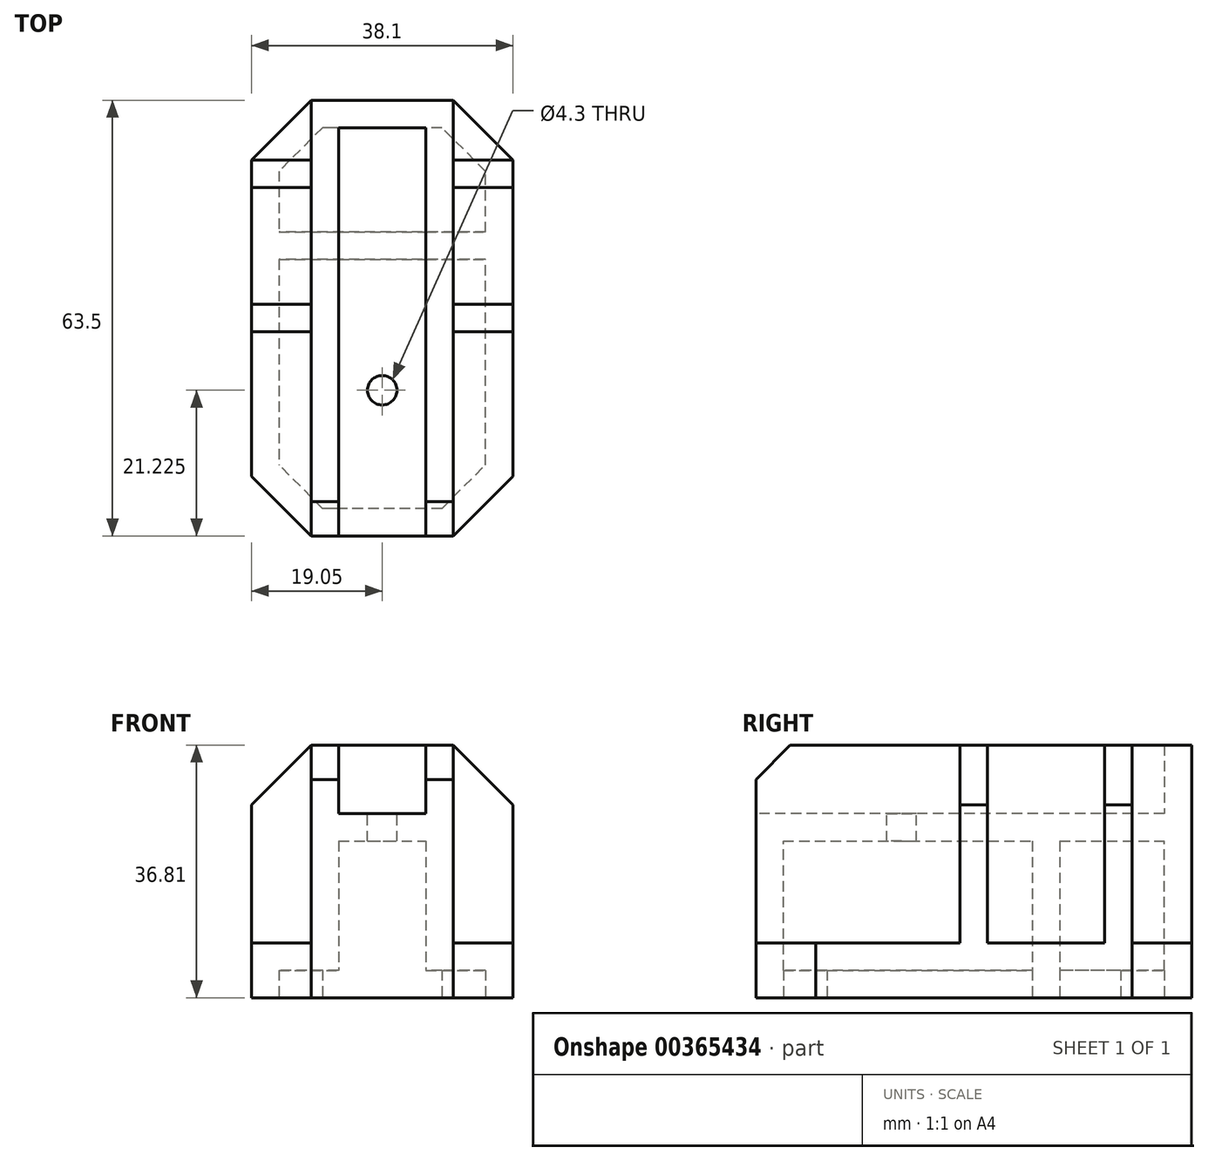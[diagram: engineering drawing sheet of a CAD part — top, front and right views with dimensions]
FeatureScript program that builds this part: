
annotation { "Feature Type Name" : "Feature", "Feature Type Description" : "" }
export const myFeature = defineFeature(function(context is Context, id is Id, definition is map)
    precondition{}
    {
        {
            var Q0;
            Q0=qCreatedBy(makeId("Front.planeOp"),FACE);
            var sketch = newSketch(context, id + "F0", { "sketchPlane" : qUnion([Q0])});
            skLineSegment(sketch, "E0.bottom", {"start": v(10.35, 0) * mm, "end": v(-10.35, 0) * mm});
            skLineSegment(sketch, "E0.top", {"start": v(10.35, 26.81) * mm, "end": v(-10.35, 26.81) * mm});
            skLineSegment(sketch, "E0.left", {"start": v(10.35, 0) * mm, "end": v(10.35, 26.81) * mm});
            skLineSegment(sketch, "E0.right", {"start": v(-10.35, 0) * mm, "end": v(-10.35, 26.81) * mm});
            skPoint(sketch, "E0.middle", {"position": v(0, 13.4) * mm});
            skLineSegment(sketch, "E1", {"start": v(-10.35, 26.81) * mm, "end": v(-10.35, 36.81) * mm});
            skLineSegment(sketch, "E2", {"start": v(-10.35, 36.81) * mm, "end": v(-6.35, 36.81) * mm});
            skLineSegment(sketch, "E3", {"start": v(-6.35, 36.81) * mm, "end": v(-6.35, 26.81) * mm});
            skLineSegment(sketch, "E4", {"start": v(0, 26.81) * mm, "end": v(0, 36.81) * mm, "construction": true});
            skLineSegment(sketch, "E5.MirrorCS", {"start": v(6.35, 36.81) * mm, "end": v(6.35, 26.81) * mm});
            skLineSegment(sketch, "E6.MirrorCS", {"start": v(10.35, 36.81) * mm, "end": v(6.35, 36.81) * mm});
            skLineSegment(sketch, "E7.MirrorCS", {"start": v(10.35, 26.81) * mm, "end": v(10.35, 36.81) * mm});
            skSolve(sketch);
        }
        {
            var Q0;
            Q0=makeQuery(id+"F0.imprint","IMPRINT",FACE,{"disambiguationData":[TD([[makeQuery(id+"F0.imprint","IMPRINT",EDGE,{"derivedFrom":sQuery(id+"F0.wireOp",EDGE,"E0.bottom")}),-1.0]])]});
            extrude(context, id + "F1", {"entities" : qUnion([Q0]), "endBound" : BoundingType.SYMMETRIC, "depth" : 63.5 * mm});
        }
        {
            var Q0;
            Q0=makeQuery(id+"F1.opExtrude","SWEPT_FACE",FACE,{"disambiguationData":[OSD([sQuery(id+"F0.wireOp",EDGE,"E0.bottom")])]});
            shell(context, id + "F2", {"entities" : qUnion([Q0]), "thickness" : 4 * mm});
        }
        {
            var Q0;
            Q0=makeQuery(id+"F1.opExtrude","CAP_FACE",FACE,{"disambiguationData":[OSD([sQuery(id+"F0.wireOp",EDGE,"E0.bottom"),sQuery(id+"F0.wireOp",EDGE,"E0.top"),sQuery(id+"F0.wireOp",EDGE,"E0.left"),sQuery(id+"F0.wireOp",EDGE,"E0.right")])],"isStart":false});
            var sketch = newSketch(context, id + "F3", { "sketchPlane" : qUnion([Q0])});
            skLineSegment(sketch, "E8.0", {"start": v(-10.35, 26.81) * mm, "end": v(-10.35, 36.81) * mm});
            skLineSegment(sketch, "E9.0", {"start": v(-10.35, 36.81) * mm, "end": v(-6.35, 36.81) * mm});
            skLineSegment(sketch, "E10.0", {"start": v(-6.35, 36.81) * mm, "end": v(-6.35, 26.81) * mm});
            skLineSegment(sketch, "E11.0", {"start": v(6.35, 36.81) * mm, "end": v(6.35, 26.81) * mm});
            skLineSegment(sketch, "E12.0", {"start": v(10.35, 36.81) * mm, "end": v(6.35, 36.81) * mm});
            skLineSegment(sketch, "E13.0", {"start": v(10.35, 26.81) * mm, "end": v(10.35, 36.81) * mm});
            skSolve(sketch);
        }
        {
            var Q0;
            {var subQ0=sQuery(id+"F3.wireOp",EDGE,"E8.0");Q0=makeQuery(id+"F3.imprint","IMPRINT",FACE,{"disambiguationData":[TD([[makeQuery(id+"F3.imprint","IMPRINT",EDGE,{"derivedFrom":subQ0}),-1.0]])]});}
            var Q1;
            {var subQ0=sQuery(id+"F3.wireOp",EDGE,"E11.0");Q1=makeQuery(id+"F3.imprint","IMPRINT",FACE,{"disambiguationData":[TD([[makeQuery(id+"F3.imprint","IMPRINT",EDGE,{"derivedFrom":subQ0}),1.0]])]});}
            var Q2;
            Q2=makeQuery(id+"F1.opExtrude","CAP_FACE",FACE,{"disambiguationData":[OSD([sQuery(id+"F0.wireOp",EDGE,"E0.bottom"),sQuery(id+"F0.wireOp",EDGE,"E0.top"),sQuery(id+"F0.wireOp",EDGE,"E0.left"),sQuery(id+"F0.wireOp",EDGE,"E0.right")])],"isStart":true});
            extrude(context, id + "F4", {"entities" : qUnion([Q0, Q1]), "operationType" : NewBodyOperationType.ADD, "endBound" : BoundingType.UP_TO_SURFACE, "oppositeDirection" : true, "endBoundEntityFace" : qUnion([Q2]), "depth" : 25 * mm});
        }
        {
            var Q0;
            Q0=qCreatedBy(makeId("Top.planeOp"),FACE);
            var sketch = newSketch(context, id + "F5", { "sketchPlane" : qUnion([Q0])});
            skLineSegment(sketch, "E14.0", {"start": v(-10.35, -31.75) * mm, "end": v(-10.35, 31.75) * mm});
            skLineSegment(sketch, "E15", {"start": v(-10.35, -31.75) * mm, "end": v(-19.05, -23.05) * mm});
            skLineSegment(sketch, "E16", {"start": v(-19.05, -23.05) * mm, "end": v(-19.05, 23.05) * mm});
            skLineSegment(sketch, "E17", {"start": v(-19.05, 23.05) * mm, "end": v(-10.35, 31.75) * mm});
            skLineSegment(sketch, "E18", {"start": v(0, 31.75) * mm, "end": v(0, -31.75) * mm, "construction": true});
            skLineSegment(sketch, "E19.MirrorCS", {"start": v(10.35, -31.75) * mm, "end": v(10.35, 31.75) * mm});
            skLineSegment(sketch, "E20.MirrorCS", {"start": v(10.35, -31.75) * mm, "end": v(19.05, -23.05) * mm});
            skLineSegment(sketch, "E21.MirrorCS", {"start": v(19.05, -23.05) * mm, "end": v(19.05, 23.05) * mm});
            skLineSegment(sketch, "E22.MirrorCS", {"start": v(19.05, 23.05) * mm, "end": v(10.35, 31.75) * mm});
            skSolve(sketch);
        }
        {
            var Q0;
            Q0 = qSketchRegion(id + "F5", true);
            extrude(context, id + "F6", {"entities" : qUnion([Q0]), "operationType" : NewBodyOperationType.ADD, "depth" : 8 * mm});
        }
        {
            var Q0;
            Q0=qCreatedBy(makeId("Front.planeOp"),FACE);
            var sketch = newSketch(context, id + "F7", { "sketchPlane" : qUnion([Q0])});
            skLineSegment(sketch, "E23.0.1", {"start": v(-10.35, 8) * mm, "end": v(-10.35, 36.81) * mm});
            skLineSegment(sketch, "E23.0.3", {"start": v(-10.35, 36.81) * mm, "end": v(-10.35, 8) * mm});
            skLineSegment(sketch, "E24.0.0", {"start": v(-10.35, 8) * mm, "end": v(-19.05, 8) * mm});
            skLineSegment(sketch, "E24.0.2", {"start": v(-19.05, 8) * mm, "end": v(-10.35, 8) * mm});
            skLineSegment(sketch, "E25", {"start": v(0, 0) * mm, "end": v(0, 36.81) * mm, "construction": true});
            skLineSegment(sketch, "E26.MirrorCS", {"start": v(19.05, 8) * mm, "end": v(10.35, 8) * mm});
            skLineSegment(sketch, "E27.MirrorCS", {"start": v(10.35, 36.81) * mm, "end": v(10.35, 8) * mm});
            skLineSegment(sketch, "E28", {"start": v(19.05, 8) * mm, "end": v(19.05, 28.11) * mm});
            skLineSegment(sketch, "E29", {"start": v(19.05, 28.1) * mm, "end": v(10.35, 36.81) * mm});
            skLineSegment(sketch, "E30.MirrorCS", {"start": v(-19.05, 8) * mm, "end": v(-19.05, 28.11) * mm});
            skLineSegment(sketch, "E31.MirrorCS", {"start": v(-19.05, 28.1) * mm, "end": v(-10.35, 36.81) * mm});
            skSolve(sketch);
        }
        {
            var Q0;
            Q0 = qSketchRegion(id + "F7", true);
            extrude(context, id + "F8", {"entities" : qUnion([Q0]), "operationType" : NewBodyOperationType.ADD, "endBound" : BoundingType.SYMMETRIC, "depth" : 4 * mm});
        }
        {
            var Q0;
            Q0=qCreatedBy(makeId("Front.planeOp"),FACE);
            var Q1;
            Q1=makeQuery(id+"F6.opExtrude","CAP_VERTEX",VERTEX,{"disambiguationData":[OSD([sQuery(id+"F5.wireOp",EDGE,"E21.MirrorCS"),sQuery(id+"F5.wireOp",EDGE,"E22.MirrorCS")])],"isStart":false});
            cPlane(context, id + "F9", {"entities" : qUnion([Q0, Q1]), "cplaneType" : CPlaneType.PLANE_POINT, "offset" : 25 * mm, "width" : 150 * mm, "height" : 150 * mm});
        }
        {
            var Q0;
            Q0=qCreatedBy(id+"F9.planeOp",FACE);
            var sketch = newSketch(context, id + "F10", { "sketchPlane" : qUnion([Q0])});
            skLineSegment(sketch, "E32.0", {"start": v(19.05, 8) * mm, "end": v(10.35, 8) * mm});
            skLineSegment(sketch, "E33.0", {"start": v(19.05, 8) * mm, "end": v(19.05, 28.11) * mm});
            skLineSegment(sketch, "E34.0", {"start": v(10.35, 36.81) * mm, "end": v(10.35, 8) * mm});
            skLineSegment(sketch, "E34.1", {"start": v(19.05, 28.1) * mm, "end": v(10.35, 36.81) * mm});
            skLineSegment(sketch, "E35.0", {"start": v(-19.05, 8) * mm, "end": v(-10.35, 8) * mm});
            skLineSegment(sketch, "E36.0", {"start": v(-10.35, 36.81) * mm, "end": v(-10.35, 8) * mm});
            skLineSegment(sketch, "E37.0", {"start": v(-19.05, 8) * mm, "end": v(-19.05, 28.11) * mm});
            skLineSegment(sketch, "E38.0", {"start": v(-19.05, 28.1) * mm, "end": v(-10.35, 36.81) * mm});
            skSolve(sketch);
        }
        {
            var Q0;
            Q0 = qSketchRegion(id + "F10", true);
            extrude(context, id + "F11", {"entities" : qUnion([Q0]), "operationType" : NewBodyOperationType.ADD, "depth" : 4 * mm});
        }
        {
            var Q0;
            Q0=makeQuery(id+"F6.boolean.opBoolean","MERGE",FACE,{"derivedFrom":[makeQuery(id+"F1.opExtrude","SWEPT_FACE",FACE,{"disambiguationData":[OSD([sQuery(id+"F0.wireOp",EDGE,"E0.bottom")])]}),makeQuery(id+"F6.opExtrude","CAP_FACE",FACE,{"disambiguationData":[OSD([sQuery(id+"F5.wireOp",EDGE,"E14.0"),sQuery(id+"F5.wireOp",EDGE,"E15"),sQuery(id+"F5.wireOp",EDGE,"E16"),sQuery(id+"F5.wireOp",EDGE,"E17")])],"isStart":true}),makeQuery(id+"F6.opExtrude","CAP_FACE",FACE,{"disambiguationData":[OSD([sQuery(id+"F5.wireOp",EDGE,"E19.MirrorCS"),sQuery(id+"F5.wireOp",EDGE,"E20.MirrorCS"),sQuery(id+"F5.wireOp",EDGE,"E21.MirrorCS"),sQuery(id+"F5.wireOp",EDGE,"E22.MirrorCS")])],"isStart":true})]});
            var sketch = newSketch(context, id + "F12", { "sketchPlane" : qUnion([Q0])});
            skLineSegment(sketch, "E39", {"start": v(8.7, -27.75) * mm, "end": v(-8.7, -27.75) * mm});
            skLineSegment(sketch, "E40", {"start": v(-8.7, -27.75) * mm, "end": v(-15.05, -21.4) * mm});
            skLineSegment(sketch, "E41", {"start": v(-15.05, -21.4) * mm, "end": v(-15.05, 21.4) * mm});
            skLineSegment(sketch, "E42", {"start": v(8.7, 27.75) * mm, "end": v(15.05, 21.4) * mm});
            skLineSegment(sketch, "E43", {"start": v(15.05, 21.4) * mm, "end": v(15.05, -21.4) * mm});
            skLineSegment(sketch, "E44", {"start": v(15.05, -21.4) * mm, "end": v(8.7, -27.75) * mm});
            skLineSegment(sketch, "E45", {"start": v(8.7, 27.75) * mm, "end": v(-8.7, 27.75) * mm});
            skLineSegment(sketch, "E46", {"start": v(-8.7, 27.75) * mm, "end": v(-15.05, 21.4) * mm});
            skSolve(sketch);
        }
        {
            var Q0;
            Q0 = qSketchRegion(id + "F12", true);
            extrude(context, id + "F13", {"entities" : qUnion([Q0]), "operationType" : NewBodyOperationType.REMOVE, "oppositeDirection" : true, "depth" : 4 * mm});
        }
        {
            var Q0;
            Q0=makeQuery(id+"F1.opExtrude","SWEPT_FACE",FACE,{"disambiguationData":[OSD([sQuery(id+"F0.wireOp",EDGE,"E0.top")])]});
            var sketch = newSketch(context, id + "F14", { "sketchPlane" : qUnion([Q0])});
            skLineSegment(sketch, "E47", {"start": v(6.35, 31.75) * mm, "end": v(6.35, 27.75) * mm});
            skLineSegment(sketch, "E48", {"start": v(6.35, 27.75) * mm, "end": v(-6.35, 27.75) * mm});
            skLineSegment(sketch, "E49", {"start": v(-6.35, 27.75) * mm, "end": v(-6.35, 31.75) * mm});
            skLineSegment(sketch, "E50", {"start": v(-6.35, 31.75) * mm, "end": v(6.35, 31.75) * mm});
            skSolve(sketch);
        }
        {
            var Q0;
            Q0=makeQuery(id+"F14.imprint","IMPRINT",FACE,{"disambiguationData":[TD([[makeQuery(id+"F14.imprint","IMPRINT",EDGE,{"derivedFrom":sQuery(id+"F14.wireOp",EDGE,"E47")}),-1.0]])]});
            var Q1;
            Q1=makeQuery(id+"F4.opExtrude","SWEPT_FACE",FACE,{"disambiguationData":[OSD([sQuery(id+"F3.wireOp",EDGE,"E9.0")])]});
            extrude(context, id + "F15", {"entities" : qUnion([Q0]), "operationType" : NewBodyOperationType.ADD, "endBound" : BoundingType.UP_TO_SURFACE, "endBoundEntityFace" : qUnion([Q1]), "depth" : 25 * mm});
        }
        {
            var Q0;
            Q0=makeQuery(id+"F4.opExtrude","CAP_EDGE",EDGE,{"disambiguationData":[OSD([sQuery(id+"F3.wireOp",EDGE,"E12.0")])],"isStart":true});
            var Q1;
            Q1=makeQuery(id+"F4.opExtrude","CAP_EDGE",EDGE,{"disambiguationData":[OSD([sQuery(id+"F3.wireOp",EDGE,"E9.0")])],"isStart":true});
            chamfer(context, id + "F16", {"entities" : qUnion([Q0, Q1]), "width" : 5 * mm, "tangentPropagation" : true});
        }
        {
            var Q0;
            Q0=makeQuery(id+"F1.opExtrude","SWEPT_FACE",FACE,{"disambiguationData":[OSD([sQuery(id+"F0.wireOp",EDGE,"E0.top")])]});
            var sketch = newSketch(context, id + "F17", { "sketchPlane" : qUnion([Q0])});
            skLineSegment(sketch, "E51", {"start": v(-6.35, -2) * mm, "end": v(6.35, -2) * mm, "construction": true});
            skLineSegment(sketch, "E52", {"start": v(-6.35, -19.05) * mm, "end": v(6.35, -19.05) * mm, "construction": true});
            skLineSegment(sketch, "E53", {"start": v(0, -2) * mm, "end": v(0, -10.53) * mm, "construction": true});
            skPoint(sketch, "E53.endSnap0", {"position": v(0, -2) * mm});
            skLineSegment(sketch, "E54", {"start": v(0, -10.53) * mm, "end": v(0, -19.05) * mm, "construction": true});
            skCircle(sketch, "E55", {"center": v(0, -10.53) * mm, "radius": 2.15 * mm});
            skSolve(sketch);
        }
        {
            var Q0;
            Q0 = qSketchRegion(id + "F17", true);
            extrude(context, id + "F18", {"entities" : qUnion([Q0]), "operationType" : NewBodyOperationType.REMOVE, "oppositeDirection" : true, "depth" : 25 * mm});
        }
        {
            var Q0;
            Q0=makeQuery(id+"F6.boolean.opBoolean","MERGE",FACE,{"derivedFrom":[makeQuery(id+"F1.opExtrude","SWEPT_FACE",FACE,{"disambiguationData":[OSD([sQuery(id+"F0.wireOp",EDGE,"E0.bottom")])]}),makeQuery(id+"F6.opExtrude","CAP_FACE",FACE,{"disambiguationData":[OSD([sQuery(id+"F5.wireOp",EDGE,"E14.0"),sQuery(id+"F5.wireOp",EDGE,"E15"),sQuery(id+"F5.wireOp",EDGE,"E16"),sQuery(id+"F5.wireOp",EDGE,"E17")])],"isStart":true}),makeQuery(id+"F6.opExtrude","CAP_FACE",FACE,{"disambiguationData":[OSD([sQuery(id+"F5.wireOp",EDGE,"E19.MirrorCS"),sQuery(id+"F5.wireOp",EDGE,"E20.MirrorCS"),sQuery(id+"F5.wireOp",EDGE,"E21.MirrorCS"),sQuery(id+"F5.wireOp",EDGE,"E22.MirrorCS")])],"isStart":true})]});
            var sketch = newSketch(context, id + "F19", { "sketchPlane" : qUnion([Q0])});
            skLineSegment(sketch, "E56.bottom", {"start": v(15.05, -8.53) * mm, "end": v(-15.05, -8.53) * mm});
            skLineSegment(sketch, "E56.top", {"start": v(15.05, -12.53) * mm, "end": v(-15.05, -12.53) * mm});
            skLineSegment(sketch, "E56.left", {"start": v(15.05, -8.53) * mm, "end": v(15.05, -12.53) * mm});
            skLineSegment(sketch, "E56.right", {"start": v(-15.05, -8.53) * mm, "end": v(-15.05, -12.53) * mm});
            skPoint(sketch, "E56.middle", {"position": v(0, -10.53) * mm});
            skLineSegment(sketch, "E57", {"start": v(0, -2) * mm, "end": v(0, -19.05) * mm, "construction": true});
            skSolve(sketch);
        }
        {
            var Q0;
            Q0 = qSketchRegion(id + "F19", true);
            var Q1;
            Q1=makeQuery(id+"F1.opExtrude","SWEPT_BODY",BODY,{"disambiguationData":[OSD([sQuery(id+"F0.wireOp",EDGE,"E0.bottom"),sQuery(id+"F0.wireOp",EDGE,"E0.top"),sQuery(id+"F0.wireOp",EDGE,"E0.left"),sQuery(id+"F0.wireOp",EDGE,"E0.right")])]});
            extrude(context, id + "F20", {"entities" : qUnion([Q0]), "operationType" : NewBodyOperationType.ADD, "endBound" : BoundingType.UP_TO_BODY, "oppositeDirection" : true, "endBoundEntityBody" : qUnion([Q1]), "depth" : 25 * mm});
        }
    });
